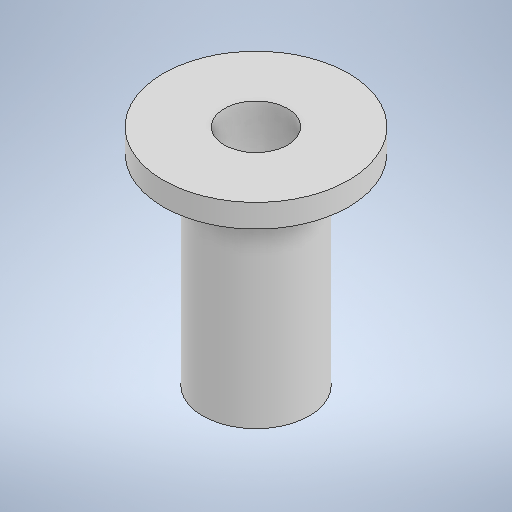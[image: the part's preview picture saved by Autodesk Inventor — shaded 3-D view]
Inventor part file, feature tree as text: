
AUTODESK INVENTOR PART (.ipt)
format: ipt  version: 2025 (Build 290162000, 162)  size: 269,824 bytes
history: native  units: mm
features: extrude x2, sketch x2
ambient origin geometry x8: Origin, YZ Plane, XZ Plane, XY Plane, X Axis, Y Axis, Z Axis, Center Point
bodies: Solid1 (feature_tree)
feature tree (4):
  extrude  "Extrusion1"  Depth=13.8mm
  extrude  "Extrusion2"  Depth=3.0mm
  sketch  "Sketch1"  dims[d0=8.2mm d1=13.8mm]
  sketch  "Sketch2"  dims[d2=29.0mm d3=0.0mm d4=24.0mm d5=3.0mm d6=0.0mm]
